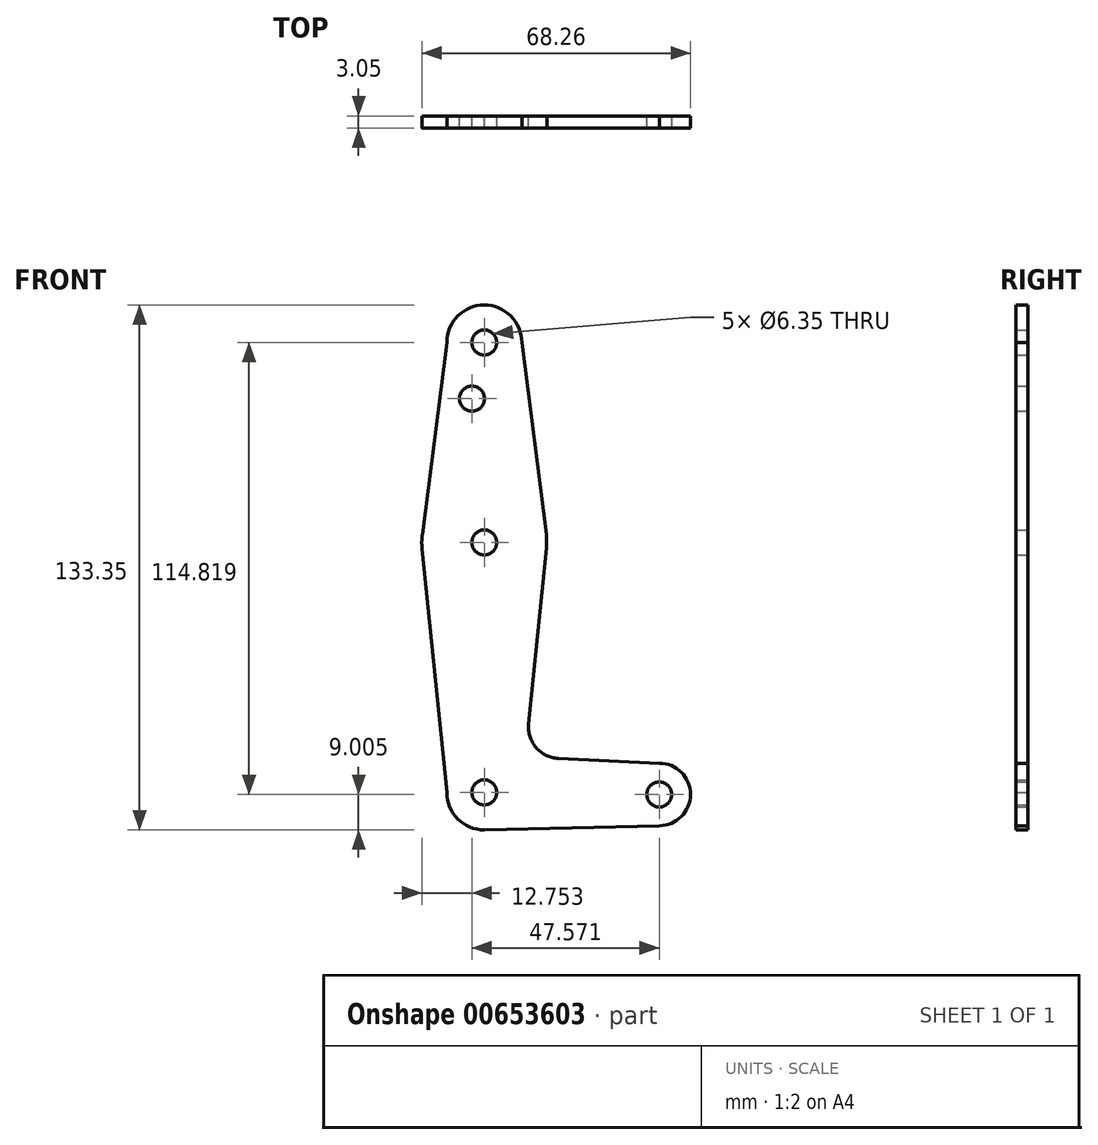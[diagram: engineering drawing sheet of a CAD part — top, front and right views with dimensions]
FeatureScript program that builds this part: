
annotation { "Feature Type Name" : "Feature", "Feature Type Description" : "" }
export const myFeature = defineFeature(function(context is Context, id is Id, definition is map)
    precondition{}
    {
        {
            var Q0;
            Q0=qCreatedBy(makeId("Front.planeOp"),FACE);
            var sketch = newSketch(context, id + "F0", { "sketchPlane" : qUnion([Q0])});
            skCircle(sketch, "E0", {"center": v(-32.63, 52.25) * mm, "radius": 9.53 * mm});
            skCircle(sketch, "E1.1.0.0", {"center": v(-32.63, 1.45) * mm, "radius": 15.88 * mm});
            skCircle(sketch, "E1.2.0.0", {"center": v(-32.63, -62.05) * mm, "radius": 9.53 * mm});
            skCircle(sketch, "E2", {"center": v(11.82, -62.56) * mm, "radius": 7.94 * mm});
            skLineSegment(sketch, "E3", {"start": v(-42.15, 52.25) * mm, "end": v(-48.37, 3.46) * mm});
            skLineSegment(sketch, "E4", {"start": v(-23.1, 52.25) * mm, "end": v(-16.88, 3.46) * mm});
            skLineSegment(sketch, "E5", {"start": v(-32.63, -71.57) * mm, "end": v(11.82, -70.5) * mm});
            skLineSegment(sketch, "E6", {"start": v(-42.15, -62.05) * mm, "end": v(-48.43, 0) * mm});
            skLineSegment(sketch, "E7", {"start": v(11.82, -54.63) * mm, "end": v(-13.8, -53.41) * mm});
            skLineSegment(sketch, "E8", {"start": v(-21.33, -44.67) * mm, "end": v(-16.82, 0) * mm});
            skArc(sketch, "E9.filletArc", {"start": v(-21.33, -44.67) * mm, "mid": v(-19.45, -50.66) * mm, "end": v(-13.8, -53.41) * mm});
            skCircle(sketch, "E10", {"center": v(-35.75, 37.98) * mm, "radius": 3.18 * mm});
            skCircle(sketch, "E11", {"center": v(-32.63, 1.45) * mm, "radius": 3.18 * mm});
            skCircle(sketch, "E12", {"center": v(-32.63, -62.05) * mm, "radius": 3.18 * mm});
            skCircle(sketch, "E13", {"center": v(11.82, -62.56) * mm, "radius": 3.18 * mm});
            skCircle(sketch, "E14", {"center": v(-32.63, 52.25) * mm, "radius": 3.18 * mm});
            skSolve(sketch);
        }
        {
            var Q0;
            {var subQ1=sQuery(id+"F0.wireOp",EDGE,"E3");Q0=makeQuery(id+"F0.imprint","IMPRINT",FACE,{"disambiguationData":[TD([[makeQuery(id+"F0.imprint","IMPRINT",EDGE,{"derivedFrom":subQ1}),1.0]])]});}
            var Q1;
            Q1=makeQuery(id+"F0.imprint","IMPRINT",FACE,{"disambiguationData":[TD([[makeQuery(id+"F0.imprint","IMPRINT",EDGE,{"derivedFrom":sQuery(id+"F0.wireOp",EDGE,"E14")}),-1.0]])]});
            var Q2;
            Q2=makeQuery(id+"F0.imprint","IMPRINT",FACE,{"disambiguationData":[TD([[makeQuery(id+"F0.imprint","IMPRINT",EDGE,{"derivedFrom":sQuery(id+"F0.wireOp",EDGE,"E11")}),-1.0]])]});
            var Q3;
            {var subQ10=sQuery(id+"F0.wireOp",EDGE,"E7");Q3=makeQuery(id+"F0.imprint","IMPRINT",FACE,{"disambiguationData":[TD([[makeQuery(id+"F0.imprint","IMPRINT",EDGE,{"derivedFrom":subQ10}),1.0]])]});}
            var Q4;
            Q4=makeQuery(id+"F0.imprint","IMPRINT",FACE,{"disambiguationData":[TD([[makeQuery(id+"F0.imprint","IMPRINT",EDGE,{"derivedFrom":sQuery(id+"F0.wireOp",EDGE,"E12")}),-1.0]])]});
            var Q5;
            Q5=makeQuery(id+"F0.imprint","IMPRINT",FACE,{"disambiguationData":[TD([[makeQuery(id+"F0.imprint","IMPRINT",EDGE,{"derivedFrom":sQuery(id+"F0.wireOp",EDGE,"E13")}),-1.0]])]});
            extrude(context, id + "F1", {"entities" : qUnion([Q0, Q1, Q2, Q3, Q4, Q5]), "depth" : 3.05 * mm, "offsetDistance" : 25.4 * mm});
        }
    });
